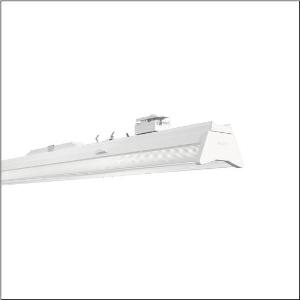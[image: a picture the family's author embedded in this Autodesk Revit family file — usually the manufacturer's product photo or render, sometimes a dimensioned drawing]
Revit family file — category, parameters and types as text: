
# Revit family: licross_r__11_performance_tw_51tm16tnt85x_6a4e
name_source: partatom
category: Lighting Fixtures
units: mm (PartAtom-declared; Revit-internal decimal feet)

## family parameters
Cut with Voids When Loaded = No
Host = Face
Light Source = No
Part Type = Normal
Room Calculation Point = No
Round Connector Dimension = Use Diameter
Shared = No

## types (1)
- --- (1 x LED 2700 K ... 6500 K, 8930 lm, 56 W, 2700K)
    Apparent Load = 56 VA
    CIE Flux Codes = 63 87 95 78 100
    Color Rendering = 80
    Color Temperature = 2700K
    Default Elevation = 1800 mm
    Description = Licross® 11 Performance TW, luminaire insert, of sheet steel, galvanised, coil coated, white, length: 1.500mm, width: 120mm, height: 123mm, LED rated luminous flux: 8.930lm, light colour: 8tw, control gear: DALI DT8, with plug, 5-pole, with phase selection, mains connection: 220..240V, AC, 50/60Hz, rated input power: 56W, halogen-free wiring, primary light control with lens, of plastic, primary optical cover: cover, of PMMA, light emission: direct/indirect distribution, primary light characteristic: symmetric, protection rating (complete): IP40, insulation class (complete): insulation class I (protective earthing), certification: CE, ENEC, VDE, UKCA, protection symbol: D if used in an environment without relevant dust loads with corresponding accessories, impact resistance: IK06, permissible ambient temperature for indoor applications: -25..+35°C, corresponds to IFS (International Featured Standards) requirements for safety and quality in the food industry, reducing of maximum allowable ambient temperature of 5°C with ceiling mounting, LABS conformity tested according to VDMA 24364:2018-05, packaging unit: 1 piece
    Height = 114 mm
    Lamp = 1 x LED 2700 K ... 6500 K
    Lamp Light Flux = 8930 lm
    Lamp Power = 56 W
    Lamp count = 1
    Length = 1500 mm
    Luminous efficacy = 159 lm/W
    Manufacturer = Siteco
    ModVariant = No
    Model = 51TM16TNT85X
    Mounting Place = Ceiling
    Mounting Type = Pendant
    Number of Poles = 1
    OnlyDefault = Yes
    Power Factor = 1
    Product Name = Licross® 11 Performance TW
    Product group = luminaire insert
    ProductGroupID = 901
    Protection Class = Protection class I
    Protection Degree = IP 40
    RLX_Detail_Level = 1
    RLX_Emergency_Light_Flux = 0 lm
    RLX_Emergency_Type = 0
    RLX_Emergency_Type_DB = No
    RlxData = <blob elided: 30377 chars, md5=c5854c0c>
    Socket = socket
    Standby Power = 0 W
    System Light Flux = 8930 lm
    System Power = 56 W
    Type Comments = individual setting: CCT=2700K
    Type Image = l_1256138.jpg
    URL = http://relux.com
    VarID = @adj_007067
    Voltage = 0 V
    Weight = 0.00 kg
    Width = 120 mm

## geometry (parser evidence)
native form markers: Blend x4, Sweep x14
no freeform markers — native parametric forms only
